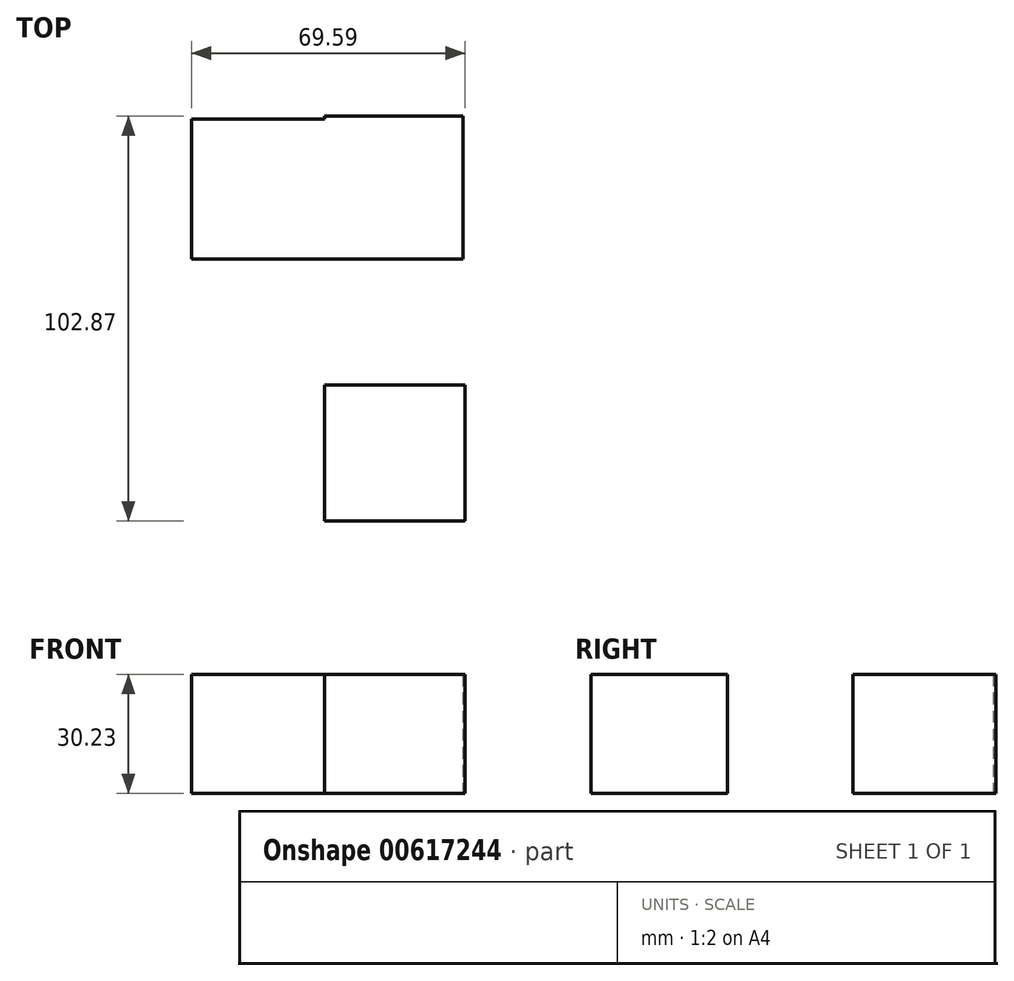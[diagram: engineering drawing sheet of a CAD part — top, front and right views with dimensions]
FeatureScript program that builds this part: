
annotation { "Feature Type Name" : "Feature", "Feature Type Description" : "" }
export const myFeature = defineFeature(function(context is Context, id is Id, definition is map)
    precondition{}
    {
        {
            var Q0;
            Q0=qCreatedBy(makeId("Top.planeOp"),FACE);
            var sketch = newSketch(context, id + "F0", { "sketchPlane" : qUnion([Q0])});
            skLineSegment(sketch, "E0.bottom", {"start": v(0, 0) * mm, "end": v(-39.73, 0) * mm});
            skLineSegment(sketch, "E0.top", {"start": v(0, 35.86) * mm, "end": v(-39.73, 35.86) * mm});
            skLineSegment(sketch, "E0.left", {"start": v(0, 0) * mm, "end": v(0, 35.86) * mm});
            skLineSegment(sketch, "E0.right", {"start": v(-39.73, 0) * mm, "end": v(-39.73, 35.86) * mm});
            skLineSegment(sketch, "E1.bottom", {"start": v(0, 0) * mm, "end": v(39.85, 0) * mm});
            skLineSegment(sketch, "E1.top", {"start": v(0, 35.86) * mm, "end": v(39.85, 35.86) * mm});
            skLineSegment(sketch, "E1.right", {"start": v(39.85, 0) * mm, "end": v(39.85, 35.86) * mm});
            skLineSegment(sketch, "E2.top", {"start": v(0, -34.15) * mm, "end": v(-39.73, -34.15) * mm});
            skLineSegment(sketch, "E2.left", {"start": v(0, 0) * mm, "end": v(0, -34.15) * mm});
            skLineSegment(sketch, "E2.right", {"start": v(-39.73, 0) * mm, "end": v(-39.73, -34.15) * mm});
            skSolve(sketch);
        }
        {
            var Q0;
            Q0=makeQuery(id+"F0.imprint","IMPRINT",FACE,{"disambiguationData":[TD([[makeQuery(id+"F0.imprint","IMPRINT",EDGE,{"derivedFrom":sQuery(id+"F0.wireOp",EDGE,"E0.top")}),1.0]])]});
            var Q1;
            Q1=makeQuery(id+"F0.imprint","IMPRINT",FACE,{"disambiguationData":[TD([[makeQuery(id+"F0.imprint","IMPRINT",EDGE,{"derivedFrom":sQuery(id+"F0.wireOp",EDGE,"E0.bottom")}),1.0]])]});
            var Q2;
            Q2=makeQuery(id+"F0.imprint","IMPRINT",FACE,{"disambiguationData":[TD([[makeQuery(id+"F0.imprint","IMPRINT",EDGE,{"derivedFrom":sQuery(id+"F0.wireOp",EDGE,"E1.bottom")}),1.0]])]});
            extrude(context, id + "F1", {"entities" : qUnion([Q0, Q1, Q2]), "depth" : 25.4 * mm, "offsetDistance" : 25.4 * mm});
        }
        {
            var Q0;
            Q0=makeQuery(id+"F1.opExtrude","CAP_FACE",FACE,{"disambiguationData":[OSD([sQuery(id+"F0.wireOp",EDGE,"E0.top"),sQuery(id+"F0.wireOp",EDGE,"E0.right"),sQuery(id+"F0.wireOp",EDGE,"E1.bottom"),sQuery(id+"F0.wireOp",EDGE,"E1.top"),sQuery(id+"F0.wireOp",EDGE,"E1.right"),sQuery(id+"F0.wireOp",EDGE,"E2.top"),sQuery(id+"F0.wireOp",EDGE,"E2.left"),sQuery(id+"F0.wireOp",EDGE,"E2.right")])],"isStart":false});
            var sketch = newSketch(context, id + "F2", { "sketchPlane" : qUnion([Q0])});
            skLineSegment(sketch, "E3.bottom", {"start": v(-39.73, -34.15) * mm, "end": v(0, -34.15) * mm});
            skLineSegment(sketch, "E3.top", {"start": v(-39.73, 0) * mm, "end": v(0, 0) * mm});
            skLineSegment(sketch, "E3.left", {"start": v(-39.73, -34.15) * mm, "end": v(-39.73, 0) * mm});
            skLineSegment(sketch, "E3.right", {"start": v(0, -34.15) * mm, "end": v(0, 0) * mm});
            skSolve(sketch);
        }
        {
            var Q0;
            Q0=makeQuery(id+"F2.imprint","IMPRINT",FACE,{"disambiguationData":[TD([[makeQuery(id+"F2.imprint","IMPRINT",EDGE,{"derivedFrom":sQuery(id+"F2.wireOp",EDGE,"E3.bottom")}),-1.0]])]});
            extrude(context, id + "F3", {"entities" : qUnion([Q0]), "operationType" : NewBodyOperationType.ADD, "depth" : 25.4 * mm, "offsetDistance" : 25.4 * mm});
        }
        {
            var Q0;
            Q0=makeQuery(id+"F1.opExtrude","SWEPT_BODY",BODY,{"disambiguationData":[OSD([sQuery(id+"F0.wireOp",EDGE,"E0.top"),sQuery(id+"F0.wireOp",EDGE,"E0.right"),sQuery(id+"F0.wireOp",EDGE,"E1.bottom"),sQuery(id+"F0.wireOp",EDGE,"E1.top"),sQuery(id+"F0.wireOp",EDGE,"E1.right"),sQuery(id+"F0.wireOp",EDGE,"E2.top"),sQuery(id+"F0.wireOp",EDGE,"E2.left"),sQuery(id+"F0.wireOp",EDGE,"E2.right")])]});
            deleteBodies(context, id + "F4", {"entities" : qUnion([Q0])});
        }
        {
            var Q0;
            Q0=qCreatedBy(makeId("Top.planeOp"),FACE);
            var sketch = newSketch(context, id + "F5", { "sketchPlane" : qUnion([Q0])});
            skLineSegment(sketch, "E4.bottom", {"start": v(0, 0) * mm, "end": v(-33.87, 0) * mm});
            skLineSegment(sketch, "E4.top", {"start": v(0, 35.63) * mm, "end": v(-33.87, 35.63) * mm});
            skLineSegment(sketch, "E4.left", {"start": v(0, 0) * mm, "end": v(0, 35.63) * mm});
            skLineSegment(sketch, "E4.right", {"start": v(-33.87, 0) * mm, "end": v(-33.87, 35.63) * mm});
            skLineSegment(sketch, "E5.bottom", {"start": v(0, 0) * mm, "end": v(35.11, 0) * mm});
            skLineSegment(sketch, "E5.top", {"start": v(0, 36.33) * mm, "end": v(35.11, 36.33) * mm});
            skLineSegment(sketch, "E5.left", {"start": v(0, 0) * mm, "end": v(0, 36.33) * mm});
            skLineSegment(sketch, "E5.right", {"start": v(35.11, 0) * mm, "end": v(35.11, 36.33) * mm});
            skLineSegment(sketch, "E6.bottom", {"start": v(0, 0) * mm, "end": v(-33.17, 0) * mm});
            skLineSegment(sketch, "E6.top", {"start": v(0, -31.95) * mm, "end": v(-33.17, -31.95) * mm});
            skLineSegment(sketch, "E6.left", {"start": v(0, 0) * mm, "end": v(0, -31.95) * mm});
            skLineSegment(sketch, "E6.right", {"start": v(-33.17, 0) * mm, "end": v(-33.17, -31.95) * mm});
            skLineSegment(sketch, "E7.bottom", {"start": v(0, 0) * mm, "end": v(35.72, 0) * mm});
            skLineSegment(sketch, "E7.top", {"start": v(0, -32.55) * mm, "end": v(35.72, -32.55) * mm});
            skLineSegment(sketch, "E7.left", {"start": v(0, 0) * mm, "end": v(0, -32.55) * mm});
            skLineSegment(sketch, "E7.right", {"start": v(35.72, 0) * mm, "end": v(35.72, -32.55) * mm});
            skLineSegment(sketch, "E8.bottom", {"start": v(-33.17, -31.95) * mm, "end": v(0, -31.95) * mm});
            skLineSegment(sketch, "E8.top", {"start": v(-33.17, -65.66) * mm, "end": v(0, -65.66) * mm});
            skLineSegment(sketch, "E8.left", {"start": v(-33.17, -31.95) * mm, "end": v(-33.17, -65.66) * mm});
            skLineSegment(sketch, "E8.right", {"start": v(0, -31.95) * mm, "end": v(0, -65.66) * mm});
            skLineSegment(sketch, "E9.bottom", {"start": v(0, -31.95) * mm, "end": v(35.72, -31.95) * mm});
            skLineSegment(sketch, "E9.top", {"start": v(0, -66.54) * mm, "end": v(35.72, -66.54) * mm});
            skLineSegment(sketch, "E9.left", {"start": v(0, -31.95) * mm, "end": v(0, -66.54) * mm});
            skLineSegment(sketch, "E9.right", {"start": v(35.72, -31.95) * mm, "end": v(35.72, -66.54) * mm});
            skSolve(sketch);
        }
        {
            var Q0;
            {var subQ3=sQuery(id+"F5.wireOp",EDGE,"E5.top");Q0=makeQuery(id+"F5.imprint","IMPRINT",FACE,{"disambiguationData":[TD([[makeQuery(id+"F5.imprint","IMPRINT",EDGE,{"derivedFrom":subQ3}),-1.0]])]});}
            var Q1;
            Q1=makeQuery(id+"F5.imprint","IMPRINT",FACE,{"disambiguationData":[TD([[makeQuery(id+"F5.imprint","IMPRINT",EDGE,{"derivedFrom":sQuery(id+"F5.wireOp",EDGE,"E4.bottom")}),-1.0]])]});
            var Q2;
            {var subQ1=sQuery(id+"F5.wireOp",EDGE,"E7.left");Q2=makeQuery(id+"F5.imprint","IMPRINT",FACE,{"disambiguationData":[TD([[makeQuery(id+"F5.imprint","IMPRINT",EDGE,{"derivedFrom":subQ1}),1.0]])]});}
            var Q3;
            Q3=makeQuery(id+"F5.imprint","IMPRINT",FACE,{"disambiguationData":[TD([[makeQuery(id+"F5.imprint","IMPRINT",EDGE,{"derivedFrom":sQuery(id+"F5.wireOp",EDGE,"E6.bottom")}),1.0]])]});
            var Q4;
            {var subQ3=sQuery(id+"F5.wireOp",EDGE,"E8.bottom");Q4=makeQuery(id+"F5.imprint","IMPRINT",FACE,{"disambiguationData":[TD([[makeQuery(id+"F5.imprint","IMPRINT",EDGE,{"derivedFrom":subQ3}),-1.0]])]});}
            var Q5;
            {var subQ1=sQuery(id+"F5.wireOp",EDGE,"E7.top");Q5=makeQuery(id+"F5.imprint","IMPRINT",FACE,{"disambiguationData":[TD([[makeQuery(id+"F5.imprint","IMPRINT",EDGE,{"derivedFrom":subQ1}),-1.0]])]});}
            extrude(context, id + "F6", {"entities" : qUnion([Q0, Q1, Q2, Q3, Q4, Q5]), "depth" : 30.23 * mm, "offsetDistance" : 25.4 * mm});
        }
    });
